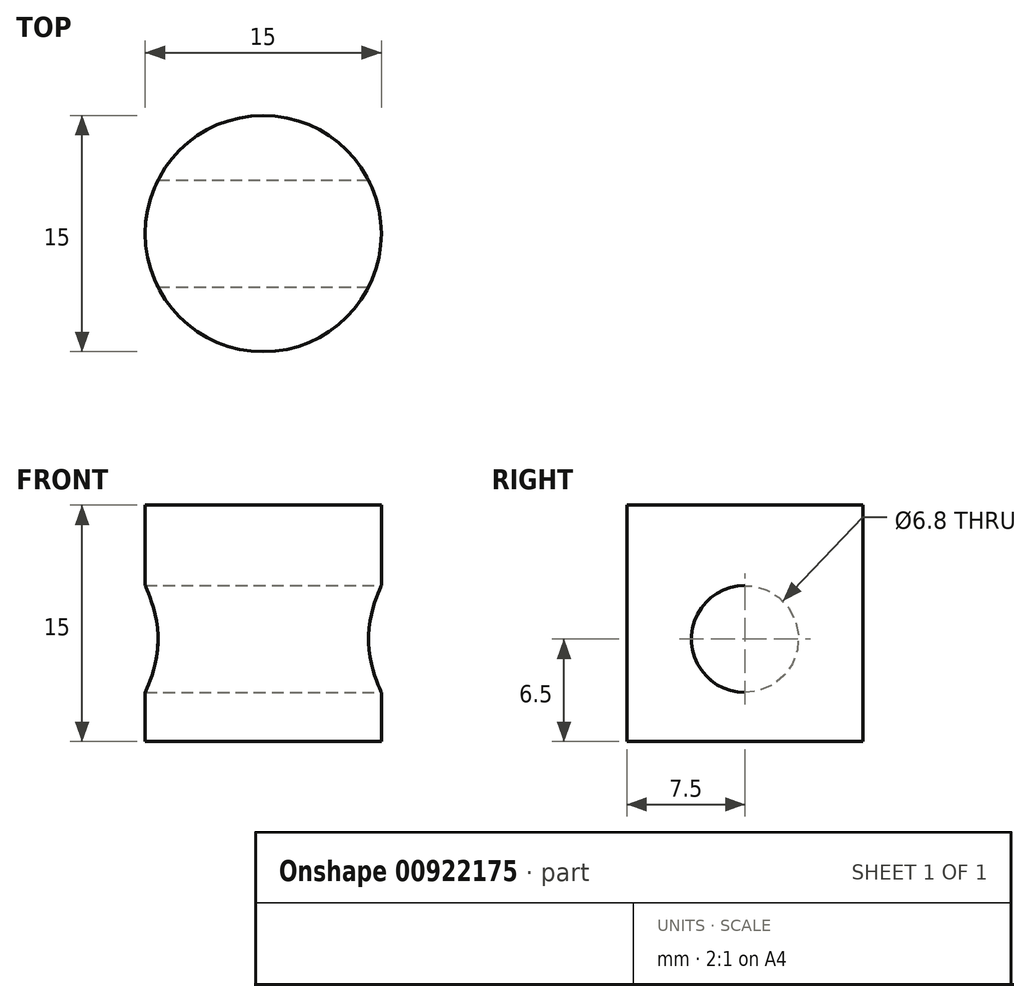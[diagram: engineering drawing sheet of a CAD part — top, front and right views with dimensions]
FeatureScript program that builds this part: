
annotation { "Feature Type Name" : "Feature", "Feature Type Description" : "" }
export const myFeature = defineFeature(function(context is Context, id is Id, definition is map)
    precondition{}
    {
        {
            var Q0;
            Q0=qCreatedBy(makeId("Top.planeOp"),FACE);
            var sketch = newSketch(context, id + "F0", { "sketchPlane" : qUnion([Q0])});
            skCircle(sketch, "E0", {"center": v(0, 0) * mm, "radius": 7.5 * mm});
            skSolve(sketch);
        }
        {
            var Q0;
            Q0 = qSketchRegion(id + "F0", true);
            extrude(context, id + "F1", {"entities" : qUnion([Q0]), "oppositeDirection" : true, "depth" : 15 * mm, "offsetDistance" : 25 * mm});
        }
        {
            var Q0;
            Q0=qCreatedBy(makeId("Right.planeOp"),FACE);
            cPlane(context, id + "F2", {"entities" : qUnion([Q0]), "cplaneType" : CPlaneType.OFFSET, "offset" : 7.5 * mm, "width" : 150 * mm, "height" : 150 * mm});
        }
        {
            var Q0;
            Q0=qCreatedBy(id+"F2.planeOp",FACE);
            var sketch = newSketch(context, id + "F3", { "sketchPlane" : qUnion([Q0])});
            skCircle(sketch, "E1", {"center": v(0, -8.5) * mm, "radius": 3.4 * mm});
            skSolve(sketch);
        }
        {
            var Q0;
            Q0=makeQuery(id+"F3.imprint","IMPRINT",FACE,{"disambiguationData":[TD([[makeQuery(id+"F3.imprint","IMPRINT",EDGE,{"derivedFrom":sQuery(id+"F3.wireOp",EDGE,"E1")}),1.0]])]});
            extrude(context, id + "F4", {"entities" : qUnion([Q0]), "operationType" : NewBodyOperationType.REMOVE, "endBound" : BoundingType.THROUGH_ALL, "oppositeDirection" : true, "depth" : 25 * mm, "offsetDistance" : 25 * mm});
        }
    });
